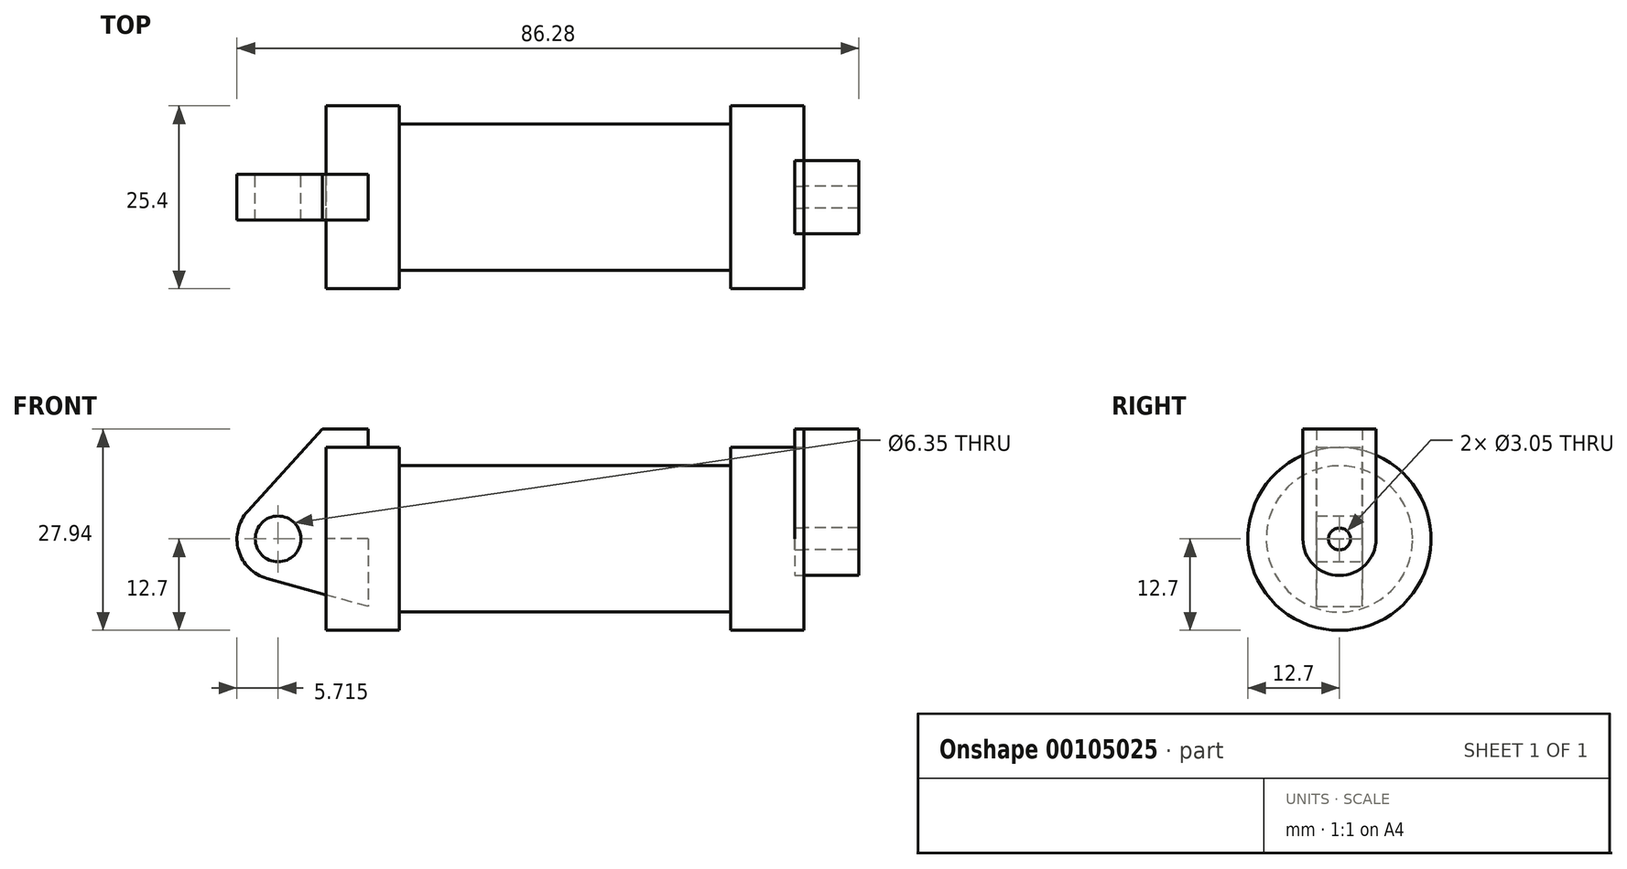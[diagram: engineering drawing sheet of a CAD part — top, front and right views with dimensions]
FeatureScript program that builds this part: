
annotation { "Feature Type Name" : "Feature", "Feature Type Description" : "" }
export const myFeature = defineFeature(function(context is Context, id is Id, definition is map)
    precondition{}
    {
        {
            var Q0;
            Q0=qCreatedBy(makeId("Front.planeOp"),FACE);
            var sketch = newSketch(context, id + "F0", { "sketchPlane" : qUnion([Q0])});
            skLineSegment(sketch, "E0", {"start": v(0, 0) * mm, "end": v(0, 12.7) * mm});
            skLineSegment(sketch, "E1", {"start": v(0, 12.7) * mm, "end": v(10.16, 12.7) * mm});
            skLineSegment(sketch, "E2", {"start": v(10.16, 12.7) * mm, "end": v(10.16, 10.16) * mm});
            skLineSegment(sketch, "E3", {"start": v(10.16, 10.16) * mm, "end": v(56.13, 10.16) * mm});
            skLineSegment(sketch, "E4", {"start": v(56.13, 10.16) * mm, "end": v(56.13, 12.7) * mm});
            skLineSegment(sketch, "E5", {"start": v(56.13, 12.7) * mm, "end": v(66.3, 12.7) * mm});
            skLineSegment(sketch, "E6", {"start": v(66.3, 12.7) * mm, "end": v(66.3, 0) * mm});
            skLineSegment(sketch, "E7", {"start": v(66.3, 0) * mm, "end": v(0, 0) * mm});
            skLineSegment(sketch, "E8", {"start": v(5.84, 15.24) * mm, "end": v(-0.5, 15.24) * mm});
            skLineSegment(sketch, "E9", {"start": v(-0.5, 15.24) * mm, "end": v(-10.88, 3.85) * mm});
            skLineSegment(sketch, "E10", {"start": v(0, 0) * mm, "end": v(-6.65, 0) * mm});
            skCircle(sketch, "E11", {"center": v(-6.65, 0) * mm, "radius": 5.72 * mm});
            skCircle(sketch, "E12", {"center": v(-6.65, 0) * mm, "radius": 3.18 * mm});
            skLineSegment(sketch, "E13", {"start": v(5.84, 15.24) * mm, "end": v(5.84, -9.4) * mm});
            skLineSegment(sketch, "E14", {"start": v(5.84, -9.4) * mm, "end": v(-8.18, -5.5) * mm});
            skSolve(sketch);
        }
        {
            var Q0;
            {var subQ0=sQuery(id+"F0.wireOp",EDGE,"E0");Q0=makeQuery(id+"F0.imprint","IMPRINT",FACE,{"disambiguationData":[TD([[makeQuery(id+"F0.imprint","IMPRINT",EDGE,{"derivedFrom":subQ0}),-1.0]])]});}
            var Q1;
            {var subQ0=sQuery(id+"F0.wireOp",EDGE,"E2");Q1=makeQuery(id+"F0.imprint","IMPRINT",FACE,{"disambiguationData":[TD([[makeQuery(id+"F0.imprint","IMPRINT",EDGE,{"derivedFrom":subQ0}),-1.0]])]});}
            var Q2;
            Q2=sQuery(id+"F0.wireOp",EDGE,"E7");
            revolve(context, id + "F1", {"entities" : qUnion([Q0, Q1]), "axis" : qUnion([Q2]), "revolveType" : RevolveType.FULL});
        }
        {
            var Q0;
            {var subQ3=sQuery(id+"F0.wireOp",EDGE,"E0");Q0=makeQuery(id+"F0.imprint","IMPRINT",FACE,{"disambiguationData":[TD([[makeQuery(id+"F0.imprint","IMPRINT",EDGE,{"derivedFrom":subQ3}),1.0]])]});}
            var Q1;
            {var subQ4=sQuery(id+"F0.wireOp",EDGE,"E12");Q1=makeQuery(id+"F0.imprint","IMPRINT",FACE,{"disambiguationData":[TD([[makeQuery(id+"F0.imprint","IMPRINT",EDGE,{"derivedFrom":subQ4}),-1.0]])]});}
            var Q2;
            {var subQ0=sQuery(id+"F0.wireOp",EDGE,"E14");Q2=makeQuery(id+"F0.imprint","IMPRINT",FACE,{"disambiguationData":[TD([[makeQuery(id+"F0.imprint","IMPRINT",EDGE,{"derivedFrom":subQ0}),-1.0]])]});}
            extrude(context, id + "F2", {"entities" : qUnion([Q0, Q1, Q2]), "endBound" : BoundingType.SYMMETRIC, "depth" : 6.35 * mm});
        }
        {
            var Q0;
            Q0=makeQuery(id+"F1.opRevolve","SWEPT_FACE",FACE,{"disambiguationData":[OSD([sQuery(id+"F0.wireOp",EDGE,"E6")])]});
            var sketch = newSketch(context, id + "F3", { "sketchPlane" : qUnion([Q0])});
            skCircle(sketch, "E15", {"center": v(0, 0) * mm, "radius": 5.08 * mm});
            skCircle(sketch, "E16", {"center": v(0, 0) * mm, "radius": 1.52 * mm});
            skLineSegment(sketch, "E17", {"start": v(-5.08, 0) * mm, "end": v(-5.08, 15.24) * mm});
            skLineSegment(sketch, "E18", {"start": v(5.08, 0) * mm, "end": v(5.08, 15.24) * mm});
            skLineSegment(sketch, "E19", {"start": v(-5.08, 15.24) * mm, "end": v(5.08, 15.24) * mm});
            skSolve(sketch);
        }
        {
            var Q0;
            {var subQ0=sQuery(id+"F3.wireOp",EDGE,"E19");Q0=makeQuery(id+"F3.imprint","IMPRINT",FACE,{"disambiguationData":[TD([[makeQuery(id+"F3.imprint","IMPRINT",EDGE,{"derivedFrom":subQ0}),-1.0]])]});}
            var Q1;
            {var subQ0=sQuery(id+"F3.wireOp",EDGE,"E17");var subQ1=sQuery(id+"F3.wireOp",EDGE,"E15");var subQ2=makeQuery(id+"F3.imprint","INTERSECT",VERTEX,{"derivedFrom":[subQ1,subQ0]});Q1=makeQuery(id+"F3.imprint","IMPRINT",FACE,{"disambiguationData":[TD([[makeQuery(id+"F3.imprint","IMPRINT",EDGE,{"disambiguationData":[TD([[subQ2,1.0]])],"derivedFrom":subQ1}),-1.0]])]});}
            var Q2;
            Q2=makeQuery(id+"F3.imprint","IMPRINT",FACE,{"disambiguationData":[TD([[makeQuery(id+"F3.imprint","IMPRINT",EDGE,{"derivedFrom":sQuery(id+"F3.wireOp",EDGE,"E16")}),-1.0]])]});
            extrude(context, id + "F4", {"entities" : qUnion([Q0, Q1, Q2]), "depth" : 7.62 * mm});
        }
        {
            var Q0;
            Q0=makeQuery(id+"F4.opExtrude","CAP_FACE",FACE,{"disambiguationData":[OSD([sQuery(id+"F3.wireOp",EDGE,"E15"),sQuery(id+"F3.wireOp",EDGE,"E16"),sQuery(id+"F3.wireOp",EDGE,"E17"),sQuery(id+"F3.wireOp",EDGE,"E18"),sQuery(id+"F3.wireOp",EDGE,"E19")])],"isStart":true});
            extrude(context, id + "F5", {"entities" : qUnion([Q0]), "depth" : 1.27 * mm});
        }
    });
